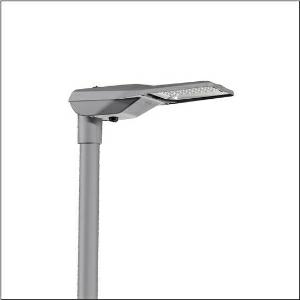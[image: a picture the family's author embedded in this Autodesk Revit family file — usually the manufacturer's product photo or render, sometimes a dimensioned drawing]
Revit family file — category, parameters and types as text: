
# Revit family: streetlight_sl_21_mini___p0_5a_5xe2v33t08hb_c971
name_source: partatom
category: Lighting Fixtures
units: mm (PartAtom-declared; Revit-internal decimal feet)

## family parameters
Cut with Voids When Loaded = No
Host = Face
Light Source = No
Part Type = Normal
Room Calculation Point = No
Round Connector Dimension = Use Diameter
Shared = No

## types (1)
- --- (1 x LED, 8890 lm, 66 W, 3000K)
    Apparent Load = 66 VA
    CIE Flux Codes = 37 73 96 100 100
    Color Rendering = 70
    Color Temperature = 3000K
    Default Elevation = 1800 mm
    Description = Streetlight SL 21 mini, mast luminaire, primary light control with lens, of PMMA, primary optical cover: cover, of toughened safety glass, transparent, light distribution: P0.5a, light emission: direct distribution, primary light characteristic: asymmetric, installation type: post-top, side-entry, LED, High Power LED, rated luminous flux: 8.890lm, luminous efficacy: 135lm/W, light colour: 730, colour temperature: 3000K, control gear: D4i, control: pre-setting: logarithmic dimming characteristic, flexible luminous flux parameterisation, time-dependent luminous flux control, constant luminous flux control, overheat protection, mains connection: 220..240V, AC, 50/60Hz, start of lifetime: 66W, end of service life: 69W, reduction: 30W, luminaire housing, of diecast aluminium, powder-coated, Siteco® metallic grey (DB 702S), corrosivity category C5 mid according to DIN EN ISO 12944, multi-level sealing system, sealing non-destructively replaceable, inclination adjustable: 0°, 5°, 10°, 15°, please order mast flange separately, length: 628mm, width: 235mm, height: 110mm, mast flange for spigot size: 42mm (side-entry): 5XC10008XM4, 60/48mm (side-entry/post-top): 5XC10108XM2, 76/60mm (side-entry/post-top): 5XC10108XM1, mounting height: 4..8m, Smart Interface below and above, protection rating (complete): IP66, insulation class (complete): insulation class II (safety insulation), certification: CE, ENEC, ENEC+, VDE, impact resistance: IK10, permissible operating ambient temperature for outdoor applications: -40..+50°C, standard-compliant lighting for roads and squares, packaging unit: 1 piece

Light Distribution: P0.5a
    Height = 110 mm
    Lamp = 1 x LED
    Lamp Light Flux = 8890 lm
    Lamp Power = 66 W
    Lamp count = 1
    Length = 625 mm
    Luminous efficacy = 135 lm/W
    Manufacturer = Siteco
    ModVariant = No
    Model = 5XE2V33T08HB
    Number of Poles = 1
    OnlyDefault = Yes
    Power Factor = 1
    Product Name = Streetlight SL 21 mini | P0.5a
    Product group = mast luminaire | pylon top
    ProductGroupID = 6100
    Protection Class = Protection class II
    Protection Degree = IP 66
    RLX_Detail_Level = 1
    RLX_Emergency_Light_Flux = 0 lm
    RLX_Emergency_Type = 0
    RLX_Emergency_Type_DB = No
    RlxData = <blob elided: 25777 chars, md5=3190b1ac>
    Socket = socket
    Standby Power = 0 W
    System Light Flux = 8890 lm
    System Power = 66 W
    Type Comments = factory setting: luminous flux: 100 % | dim-lin: 254 | 670 mA
    Type Image = l_1003514.jpg
    URL = http://relux.com
    VarID = @adj_069768
    Voltage = 0 V
    Weight = 0.00 kg
    Width = 234 mm

## geometry (parser evidence)
native form markers: Blend x4, Sweep x10
no freeform markers — native parametric forms only
